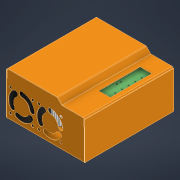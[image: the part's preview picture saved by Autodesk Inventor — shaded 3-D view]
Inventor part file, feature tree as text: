
AUTODESK INVENTOR PART (.ipt)
format: ipt  version: 2022 (Build 260153000, 153)  size: 3,180,544 bytes
history: native  units: in
note: dims shown in document units (in); Inventor stores cm internally (conversion verified against a paired STEP export)
features: other x13, sheet_metal_op x12, sketch x9, plane x2, pattern_linear x2, mirror x1, hole x1, projected_geometry x1
ambient origin geometry x8: Origin, YZ Plane, XZ Plane, XY Plane, X Axis, Y Axis, Z Axis, Center Point
bodies: Solid1 (feature_tree), Solid2 (feature_tree), Solid3 (feature_tree), Solid4 (feature_tree), Solid5 (feature_tree)
feature tree (41):
  other  "Inner Assembly.iam"
  other  "heatsink.ipt:1"
  other  "PCB v1.iam:1::HV servo drive v1 PCB.ipt:1"
  other  "SanAce_9GA_40x20_RBD.ipt:1"
  plane  "Work Plane1"
  sheet_metal_op  "Face1"
  sheet_metal_op  "Flange1"
  sheet_metal_op  "Flange2"
  sketch  "Sketch4"  dims[d4=0.1in]
  sheet_metal_op  "Face3"
  plane  "Work Plane2"
  mirror  "Mirror1"
  sheet_metal_op  "Contour Flange1"
  sketch  "Sketch6"  dims[d6=0.03in]
  hole  "Hole1"  [1 undecoded]
  pattern_linear  "Rectangular Pattern1"  Spacing1=1.0in  [1 undecoded]
  pattern_linear  "Rectangular Pattern2"  Spacing1=-0.45in  [1 undecoded]
  sketch  "Sketch1"  dims[d0=0.3937in d1=0.06in]
  other  "Plate1"
  sketch  "Sketch2"  dims[d2=0.1in]
  other  "Plate2"
  sheet_metal_op  "Bend1"
  sheet_metal_op  "Corner1"
  sketch  "Sketch3"  dims[d3=1.0in]
  other  "Plate3"
  sheet_metal_op  "Bend2"
  sheet_metal_op  "Corner2"
  other  "Plate5"
  sheet_metal_op  "Bend4"
  sketch  "Sketch5"  dims[d5=0.03in]
  other  "Plate6"
  sheet_metal_op  "Bend5"
  sheet_metal_op  "Corner3"
  sketch  "Sketch7"  dims[d7=0.015in]
  sketch  "Sketch8"  dims[d8=0.06in]
  sketch  "Sketch9"  dims[d9=0.03in d10=1.0in d11=90.0deg d12=0.03in d13=-0.45in d14=0.12in d15=0.03in d16=0.03in d17=0.03in d18=0.015in d19=0.06in d20=0.03in d21=1.0in d22=90.0deg d23=0.03in d24=-0.2in d25=0.12in d26=0.03in d27=0.03in d28=0.2362in d29=0.03in d30=0.03in d31=0.03in d32=0.03in d33=0.03in d34=0.03in d35=0.03in d36=0.03in d37=135.0deg d38=0.5in d39=1.25in d40=0.3937in d41=0.3937in d47=0.005in d48=0.005in d49=0.03in d50=0.03in d51=0.015in d52=0.06in d53=0.03in d54=0.03in d55=0.03in d56=0.015in d57=0.06in d58=0.03in d59=5.037in d60=0.03in d61=0.03in d62=0.12in d63=0.03in d64=0.03in d65=1.2598in d66=1.5748in d67=0.04in d68=0.0394in d69=0.45in d70=0.2983in d71=1.1811in d73=360.0deg d75=0.4in d76=0.1575in d77=0.236in d78=0.119in d79=0.25in d80=0.5635in d81=0.03in d82=0.8108in d83=0.03in d84=0.0in d85=0.7874in d87=1.6142in d88=0.2in d89=0.15in d90=0.15in d91=0.03in d92=0.0in d93=0.0344in d94=3.937in d96=0.3in d97=0.31in d98=0.31in d99=0.02in d100=0.03in d101=0.0in d102=0.6693in d103=2.3622in d104=0.03in d105=0.0in]
  projected_geometry  "Projected Loop1"
  other  "Cut1"
  other  "Cut2"
  other  "Cut3"
  other  "Cut4"
note: 3 required parameter values undecoded (feature->parameter linkage not recoverable at this tier; creation-order binding heuristic only, values carry confidence <= 0.55)
